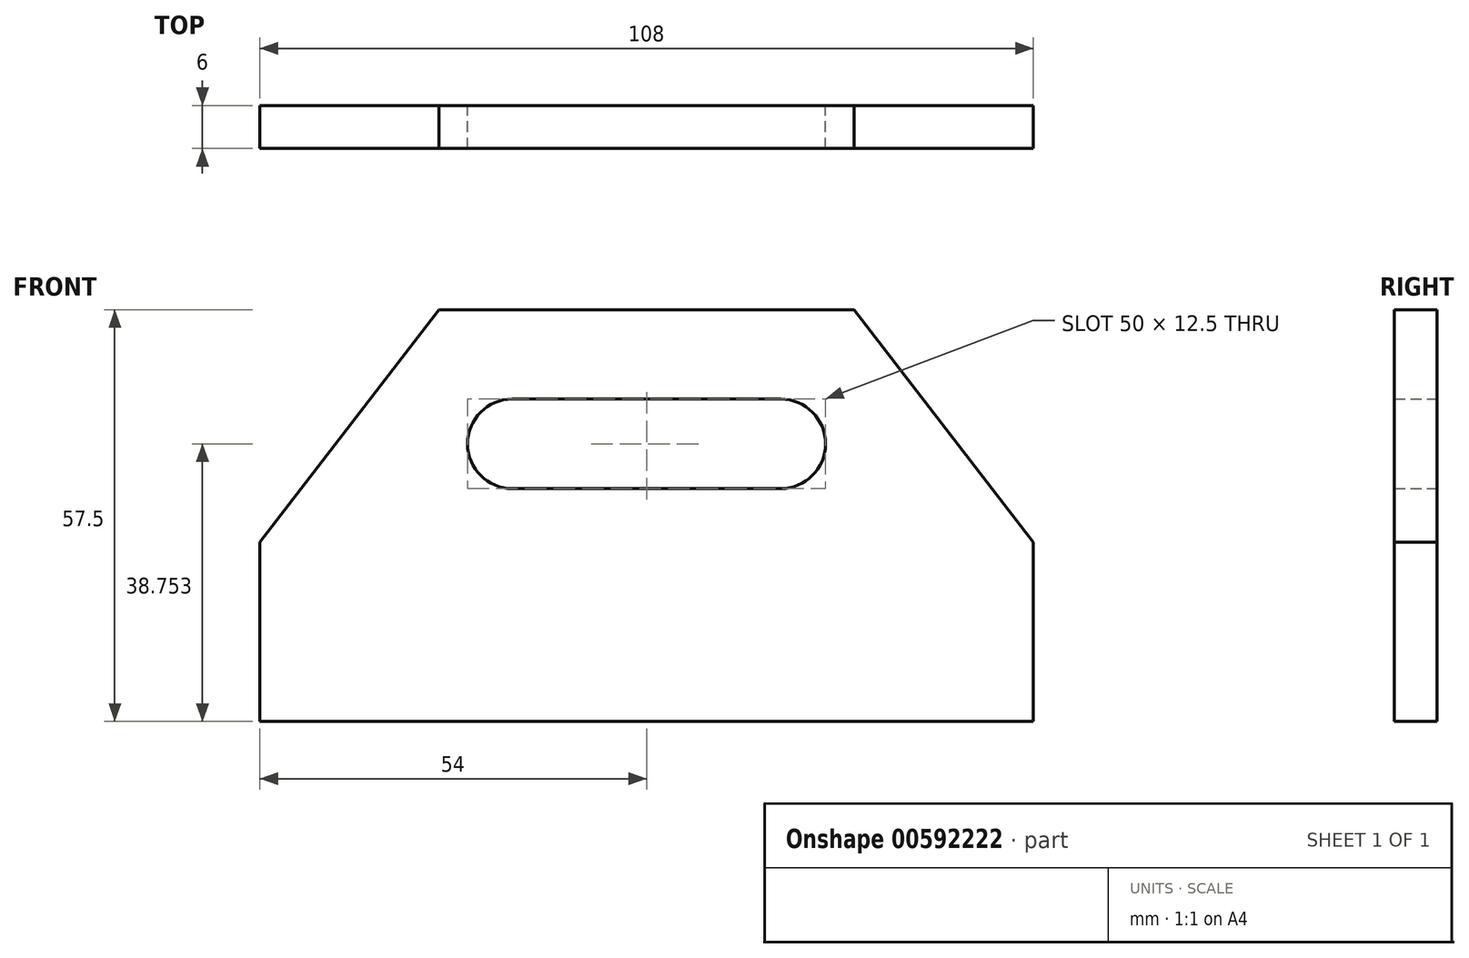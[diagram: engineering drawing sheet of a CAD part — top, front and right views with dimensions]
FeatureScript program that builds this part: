
annotation { "Feature Type Name" : "Feature", "Feature Type Description" : "" }
export const myFeature = defineFeature(function(context is Context, id is Id, definition is map)
    precondition{}
    {
        {
            var Q0;
            Q0=qCreatedBy(makeId("Front.planeOp"),FACE);
            var sketch = newSketch(context, id + "F0", { "sketchPlane" : qUnion([Q0])});
            skLineSegment(sketch, "E0", {"start": v(-29, 65.72) * mm, "end": v(29, 65.72) * mm});
            skLineSegment(sketch, "E1", {"start": v(29, 65.72) * mm, "end": v(54, 33.22) * mm});
            skLineSegment(sketch, "E2", {"start": v(54, 33.22) * mm, "end": v(54, 8.22) * mm});
            skLineSegment(sketch, "E3", {"start": v(54, 8.22) * mm, "end": v(-54, 8.22) * mm});
            skLineSegment(sketch, "E4", {"start": v(-54, 8.22) * mm, "end": v(-54, 33.22) * mm});
            skLineSegment(sketch, "E5", {"start": v(-54, 33.22) * mm, "end": v(-29, 65.72) * mm});
            skLineSegment(sketch, "E6", {"start": v(-18.75, 53.22) * mm, "end": v(18.75, 53.22) * mm});
            skLineSegment(sketch, "E7", {"start": v(18.75, 40.72) * mm, "end": v(-18.75, 40.72) * mm});
            skArc(sketch, "E8", {"start": v(18.75, 40.72) * mm, "mid": v(25, 46.97) * mm, "end": v(18.75, 53.22) * mm});
            skArc(sketch, "E9", {"start": v(-18.75, 53.22) * mm, "mid": v(-25, 46.97) * mm, "end": v(-18.75, 40.72) * mm});
            skSolve(sketch);
        }
        {
            var Q0;
            Q0=makeQuery(id+"F0.imprint","IMPRINT",FACE,{"disambiguationData":[TD([[makeQuery(id+"F0.imprint","IMPRINT",EDGE,{"derivedFrom":sQuery(id+"F0.wireOp",EDGE,"E0")}),-1.0]])]});
            extrude(context, id + "F1", {"entities" : qUnion([Q0]), "depth" : 6 * mm, "offsetDistance" : 25 * mm});
        }
    });
